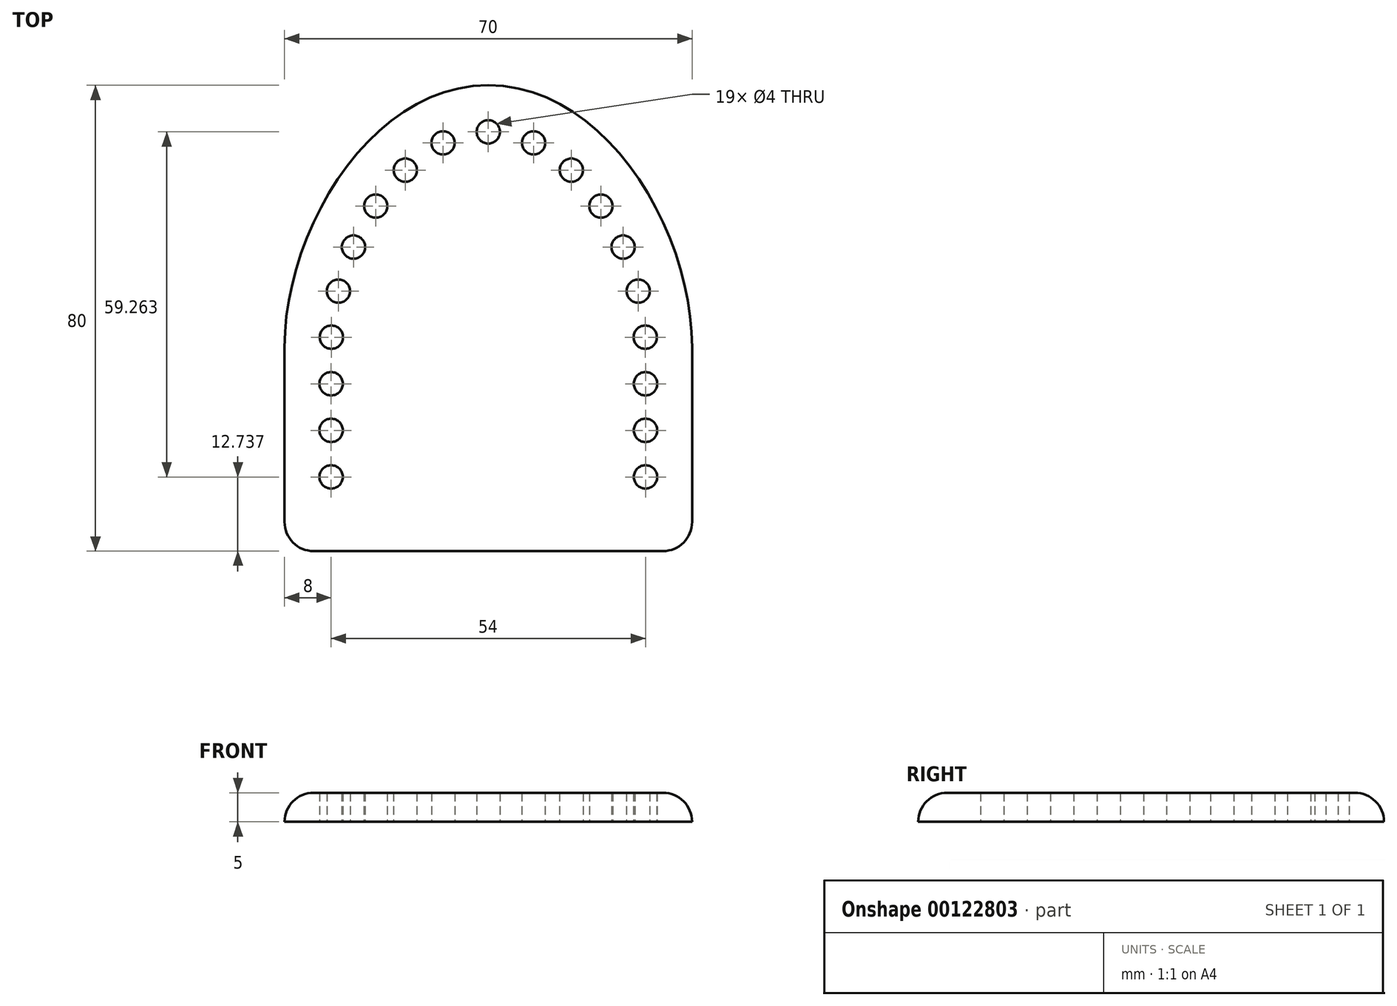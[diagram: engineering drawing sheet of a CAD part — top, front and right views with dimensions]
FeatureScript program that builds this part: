
annotation { "Feature Type Name" : "Feature", "Feature Type Description" : "" }
export const myFeature = defineFeature(function(context is Context, id is Id, definition is map)
    precondition{}
    {
        {
            var Q0;
            Q0=qCreatedBy(makeId("Top.planeOp"),FACE);
            var sketch = newSketch(context, id + "F0", { "sketchPlane" : qUnion([Q0])});
            skLineSegment(sketch, "E0.top", {"start": v(-35, -35) * mm, "end": v(35, -35) * mm});
            skPoint(sketch, "E0.middle", {"position": v(0, 13.14) * mm});
            skPoint(sketch, "E1", {"position": v(0, 0) * mm});
            skCircle(sketch, "E2", {"center": v(0, 0) * mm, "radius": 35 * mm});
            skPoint(sketch, "E3.visualSharp", {"position": v(-35, -35) * mm});
            skPoint(sketch, "E4.visualSharp", {"position": v(35, -35) * mm});
            skPoint(sketch, "E5", {"position": v(-35, 0) * mm});
            skPoint(sketch, "E6", {"position": v(35, 0) * mm});
            skFitSpline(sketch, "E7", {"points": [v(0, 45) * mm, v(-35, 0) * mm], "startDerivative": vector(-60.6, 0) * mm, "endDerivative": vector(0, -60.15) * mm});
            skLineSegment(sketch, "E8", {"start": v(-35, 0) * mm, "end": v(-35, -35) * mm});
            skLineSegment(sketch, "E9", {"start": v(35, 0) * mm, "end": v(35, -35) * mm});
            skFitSpline(sketch, "E10.MirrorCS", {"points": [v(0, 45) * mm, v(35, 0) * mm], "startDerivative": vector(60.6, 0) * mm, "endDerivative": vector(0, -60.15) * mm});
            skFitSpline(sketch, "E11.0", {"points": [v(0, 37) * mm, v(-0.85, 37) * mm, v(-2.51, 36.87) * mm, v(-4.95, 36.3) * mm, v(-7.36, 35.37) * mm, v(-10.54, 33.64) * mm, v(-14.42, 30.55) * mm, v(-18.67, 25.54) * mm, v(-22.24, 19.56) * mm, v(-24.95, 13) * mm, v(-26.62, 6.3) * mm, v(-27, 2.01) * mm, v(-27, 0) * mm]});
            skPoint(sketch, "E12", {"position": v(0, 37) * mm});
            skPoint(sketch, "E13", {"position": v(-7.77, 35.11) * mm});
            skPoint(sketch, "E14", {"position": v(-14.26, 30.43) * mm});
            skPoint(sketch, "E15", {"position": v(-19.34, 24.24) * mm});
            skPoint(sketch, "E16", {"position": v(-23.15, 17.21) * mm});
            skPoint(sketch, "E17", {"position": v(-25.74, 9.64) * mm});
            skLineSegment(sketch, "E18", {"start": v(-27, 0) * mm, "end": v(-27, -35) * mm});
            skPoint(sketch, "E19", {"position": v(-26.96, 1.74) * mm});
            skPoint(sketch, "E20", {"position": v(-27, -6.26) * mm});
            skPoint(sketch, "E21", {"position": v(-27, -14.26) * mm});
            skPoint(sketch, "E22", {"position": v(-27, -22.26) * mm});
            skPoint(sketch, "E23", {"position": v(-27, -30.26) * mm});
            skLineSegment(sketch, "E24.MirrorCS", {"start": v(27, 0) * mm, "end": v(27, -35) * mm});
            skPoint(sketch, "E25.MirrorP", {"position": v(7.77, 35.11) * mm});
            skPoint(sketch, "E26.MirrorP", {"position": v(14.26, 30.43) * mm});
            skPoint(sketch, "E27.MirrorP", {"position": v(19.34, 24.24) * mm});
            skPoint(sketch, "E28.MirrorP", {"position": v(23.15, 17.21) * mm});
            skPoint(sketch, "E29.MirrorP", {"position": v(25.74, 9.64) * mm});
            skPoint(sketch, "E30.MirrorP", {"position": v(26.96, 1.74) * mm});
            skPoint(sketch, "E31.MirrorP", {"position": v(27, -6.26) * mm});
            skPoint(sketch, "E32.MirrorP", {"position": v(27, -14.26) * mm});
            skPoint(sketch, "E33.MirrorP", {"position": v(27, -22.26) * mm});
            skPoint(sketch, "E34.MirrorP", {"position": v(27, -30.26) * mm});
            skFitSpline(sketch, "E35.0", {"points": [v(0, 37) * mm, v(0.85, 37) * mm, v(2.51, 36.87) * mm, v(4.95, 36.3) * mm, v(7.36, 35.37) * mm, v(10.54, 33.64) * mm, v(14.42, 30.55) * mm, v(18.67, 25.54) * mm, v(22.24, 19.56) * mm, v(24.95, 13) * mm, v(26.62, 6.3) * mm, v(27, 2.01) * mm, v(27, 0) * mm]});
            skSolve(sketch);
        }
        {
            var Q0;
            Q0=qSketchRegion(id+"F0",true);
            var Q1;
            {var subQ0=sQuery(id+"F0.wireOp",EDGE,"E35.0");var subQ1=sQuery(id+"F0.wireOp",EDGE,"E2");var subQ2=makeQuery(id+"F0.imprint","INTERSECT",VERTEX,{"derivedFrom":[subQ1,subQ0]});Q1=makeQuery(id+"F0.imprint","IMPRINT",FACE,{"disambiguationData":[TD([[makeQuery(id+"F0.imprint","IMPRINT",EDGE,{"disambiguationData":[TD([[subQ2,-1.0]])],"derivedFrom":subQ1}),-1.0]])]});}
            extrude(context, id + "F1", {"entities" : qUnion([Q0, Q1]), "depth" : 5 * mm});
        }
        {
            var Q0;
            Q0=sQuery(id+"F0.wireOp",VERTEX,"E12");
            var Q1;
            Q1=sQuery(id+"F0.wireOp",VERTEX,"E13");
            var Q2;
            Q2=sQuery(id+"F0.wireOp",VERTEX,"E14");
            var Q3;
            Q3=sQuery(id+"F0.wireOp",VERTEX,"E15");
            var Q4;
            Q4=sQuery(id+"F0.wireOp",VERTEX,"E16");
            var Q5;
            Q5=sQuery(id+"F0.wireOp",VERTEX,"E17");
            var Q6;
            Q6=sQuery(id+"F0.wireOp",VERTEX,"E19");
            var Q7;
            Q7=sQuery(id+"F0.wireOp",VERTEX,"E20");
            var Q8;
            Q8=sQuery(id+"F0.wireOp",VERTEX,"E21");
            var Q9;
            Q9=sQuery(id+"F0.wireOp",VERTEX,"E22");
            var Q10;
            Q10=sQuery(id+"F0.wireOp",VERTEX,"E25.MirrorP");
            var Q11;
            Q11=sQuery(id+"F0.wireOp",VERTEX,"E26.MirrorP");
            var Q12;
            Q12=sQuery(id+"F0.wireOp",VERTEX,"E27.MirrorP");
            var Q13;
            Q13=sQuery(id+"F0.wireOp",VERTEX,"E28.MirrorP");
            var Q14;
            Q14=sQuery(id+"F0.wireOp",VERTEX,"E29.MirrorP");
            var Q15;
            Q15=sQuery(id+"F0.wireOp",VERTEX,"E30.MirrorP");
            var Q16;
            Q16=sQuery(id+"F0.wireOp",VERTEX,"E31.MirrorP");
            var Q17;
            Q17=sQuery(id+"F0.wireOp",VERTEX,"E32.MirrorP");
            var Q18;
            Q18=sQuery(id+"F0.wireOp",VERTEX,"E33.MirrorP");
            var Q19;
            Q19=makeQuery(id+"F1.opExtrude","SWEPT_BODY",BODY,{"disambiguationData":[OSD([sQuery(id+"F0.wireOp",EDGE,"E0.top"),sQuery(id+"F0.wireOp",EDGE,"E2"),sQuery(id+"F0.wireOp",EDGE,"E7"),sQuery(id+"F0.wireOp",EDGE,"E8"),sQuery(id+"F0.wireOp",EDGE,"E9"),sQuery(id+"F0.wireOp",EDGE,"E10.MirrorCS"),sQuery(id+"F0.wireOp",EDGE,"E11.0"),sQuery(id+"F0.wireOp",EDGE,"E35.0")])]});
            hole(context, id + "F2", {"style" : HoleStyle.SIMPLE, "endStyle" : HoleEndStyle.THROUGH, "oppositeDirection" : true, "holeDiameter" : 4 * mm, "startFromSketch" : true, "locations" : qUnion([Q0, Q1, Q2, Q3, Q4, Q5, Q6, Q7, Q8, Q9, Q10, Q11, Q12, Q13, Q14, Q15, Q16, Q17, Q18]), "scope" : qUnion([Q19]), "isTappedThrough" : true});
        }
        {
            var Q0;
            Q0=makeQuery(id+"F1.opExtrude","SWEPT_EDGE",EDGE,{"disambiguationData":[OSD([sQuery(id+"F0.wireOp",EDGE,"E0.top"),sQuery(id+"F0.wireOp",EDGE,"E8")])]});
            var Q1;
            Q1=makeQuery(id+"F1.opExtrude","SWEPT_EDGE",EDGE,{"disambiguationData":[OSD([sQuery(id+"F0.wireOp",EDGE,"E0.top"),sQuery(id+"F0.wireOp",EDGE,"E9")])]});
            var Q2;
            Q2=makeQuery(id+"F1.opExtrude","CAP_EDGE",EDGE,{"disambiguationData":[OSD([sQuery(id+"F0.wireOp",EDGE,"E8")])],"isStart":false});
            var Q3;
            Q3=makeQuery(id+"F1.opExtrude","CAP_EDGE",EDGE,{"disambiguationData":[OSD([sQuery(id+"F0.wireOp",EDGE,"E0.top")])],"isStart":false});
            fillet(context, id + "F3", {"entities" : qUnion([Q0, Q1, Q2, Q3]), "radius" : 5 * mm, "tangentPropagation" : true, "allowEdgeOverflow" : false});
        }
    });
